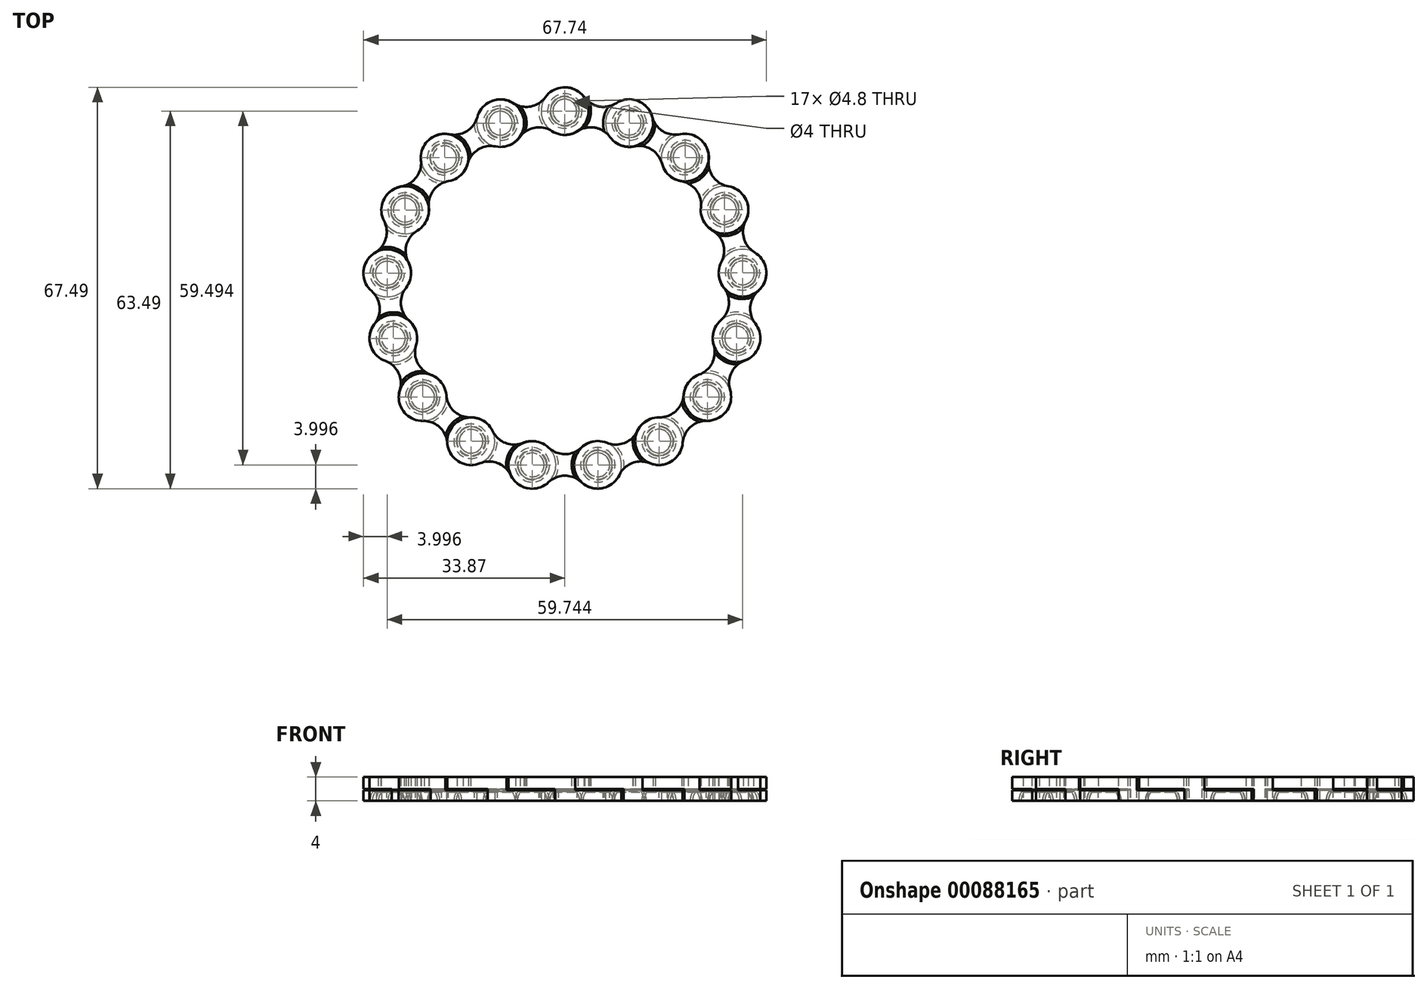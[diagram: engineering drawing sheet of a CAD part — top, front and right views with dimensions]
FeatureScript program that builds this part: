
annotation { "Feature Type Name" : "Feature", "Feature Type Description" : "" }
export const myFeature = defineFeature(function(context is Context, id is Id, definition is map)
    precondition{}
    {
        {
            var Q0;
            Q0=qCreatedBy(makeId("Top.planeOp"),FACE);
            var sketch = newSketch(context, id + "F0", { "sketchPlane" : qUnion([Q0])});
            skCircle(sketch, "E0", {"center": v(0, 0) * mm, "radius": 30 * mm, "construction": true});
            skCircle(sketch, "E1", {"center": v(0, 30) * mm, "radius": 4 * mm});
            skCircle(sketch, "E2", {"center": v(10.81, 27.98) * mm, "radius": 4 * mm});
            skArc(sketch, "E3", {"start": v(3.24, 32.35) * mm, "mid": v(5.74, 30.77) * mm, "end": v(8.64, 31.34) * mm});
            skArc(sketch, "E4", {"start": v(7.58, 25.63) * mm, "mid": v(5.08, 27.21) * mm, "end": v(2.17, 26.64) * mm});
            skCircle(sketch, "E5", {"center": v(0, 30) * mm, "radius": 2 * mm});
            skCircle(sketch, "E6", {"center": v(10.81, 27.98) * mm, "radius": 2 * mm});
            skSolve(sketch);
        }
        {
            var Q0;
            Q0 = qSketchRegion(id + "F0", true);
            var Q1;
            Q1=makeQuery(id+"F0.imprint","IMPRINT",FACE,{"disambiguationData":[TD([[makeQuery(id+"F0.imprint","IMPRINT",EDGE,{"derivedFrom":sQuery(id+"F0.wireOp",EDGE,"E6")}),1.0]])]});
            extrude(context, id + "F1", {"entities" : qUnion([Q0, Q1]), "depth" : 2 * mm});
        }
        {
            var Q0;
            Q0=makeQuery(id+"F0.imprint","IMPRINT",FACE,{"disambiguationData":[TD([[makeQuery(id+"F0.imprint","IMPRINT",EDGE,{"derivedFrom":sQuery(id+"F0.wireOp",EDGE,"E6")}),-1.0]])]});
            var Q1;
            Q1=makeQuery(id+"F0.imprint","IMPRINT",FACE,{"disambiguationData":[TD([[makeQuery(id+"F0.imprint","IMPRINT",EDGE,{"derivedFrom":sQuery(id+"F0.wireOp",EDGE,"E6")}),1.0]])]});
            var Q2;
            {var subQ0=sQuery(id+"F0.wireOp",EDGE,"E3");Q2=makeQuery(id+"F0.imprint","IMPRINT",FACE,{"disambiguationData":[TD([[makeQuery(id+"F0.imprint","IMPRINT",EDGE,{"derivedFrom":subQ0}),-1.0]])]});}
            extrude(context, id + "F2", {"entities" : qUnion([Q0, Q1, Q2]), "operationType" : NewBodyOperationType.ADD, "depth" : 4 * mm});
        }
        {
            var Q0;
            Q0=makeQuery(id+"F0.imprint","IMPRINT",FACE,{"disambiguationData":[TD([[makeQuery(id+"F0.imprint","IMPRINT",EDGE,{"derivedFrom":sQuery(id+"F0.wireOp",EDGE,"E6")}),1.0]])]});
            var sketch = newSketch(context, id + "F3", { "sketchPlane" : qUnion([Q0])});
            skArc(sketch, "E7", {"start": v(13.31, 27.98) * mm, "mid": v(10.81, 30.48) * mm, "end": v(8.31, 27.98) * mm});
            skLineSegment(sketch, "E8", {"start": v(13.31, 27.98) * mm, "end": v(8.31, 27.98) * mm});
            skSolve(sketch);
        }
        {
            var Q0;
            Q0=makeQuery(id+"F0.imprint","IMPRINT",FACE,{"disambiguationData":[TD([[makeQuery(id+"F0.imprint","IMPRINT",EDGE,{"derivedFrom":sQuery(id+"F0.wireOp",EDGE,"E6")}),-1.0]])]});
            extrude(context, id + "F4", {"entities" : qUnion([Q0]), "operationType" : NewBodyOperationType.REMOVE, "depth" : 2 * mm});
        }
        {
            var Q0;
            Q0 = qSketchRegion(id + "F3", true);
            var Q1;
            Q1=sQuery(id+"F3.wireOp",EDGE,"E8");
            revolve(context, id + "F5", {"operationType" : NewBodyOperationType.ADD, "entities" : qUnion([Q0]), "axis" : qUnion([Q1]), "revolveType" : RevolveType.ONE_DIRECTION, "oppositeDirection" : true, "angle" : 180 * degree});
        }
        {
            var Q0;
            Q0=makeQuery(id+"F2.opExtrude","CAP_FACE",FACE,{"disambiguationData":[OSD([sQuery(id+"F0.wireOp",EDGE,"E1"),sQuery(id+"F0.wireOp",EDGE,"E2"),sQuery(id+"F0.wireOp",EDGE,"E3"),sQuery(id+"F0.wireOp",EDGE,"E4")])],"isStart":false});
            var sketch = newSketch(context, id + "F6", { "sketchPlane" : qUnion([Q0])});
            skArc(sketch, "E9", {"start": v(13.31, 27.98) * mm, "mid": v(10.81, 30.48) * mm, "end": v(8.31, 27.98) * mm});
            skLineSegment(sketch, "E10", {"start": v(13.31, 27.98) * mm, "end": v(8.31, 27.98) * mm});
            skSolve(sketch);
        }
        {
            var Q0;
            {var subQ0=sQuery(id+"F0.wireOp",EDGE,"E3");Q0=makeQuery(id+"F0.imprint","IMPRINT",FACE,{"disambiguationData":[TD([[makeQuery(id+"F0.imprint","IMPRINT",EDGE,{"derivedFrom":subQ0}),-1.0]])]});}
            var sketch = newSketch(context, id + "F7", { "sketchPlane" : qUnion([Q0])});
            skCircle(sketch, "E11.0", {"center": v(10.81, 27.98) * mm, "radius": 4 * mm});
            skArc(sketch, "E12.0", {"start": v(7.58, 25.63) * mm, "mid": v(5.08, 27.21) * mm, "end": v(2.17, 26.64) * mm});
            skArc(sketch, "E13.0", {"start": v(3.24, 32.35) * mm, "mid": v(5.74, 30.77) * mm, "end": v(8.64, 31.34) * mm});
            skArc(sketch, "E14", {"start": v(7.45, 30.83) * mm, "mid": v(6.49, 28.79) * mm, "end": v(6.66, 26.54) * mm});
            skSolve(sketch);
        }
        {
            var Q0;
            {var subQ5=sQuery(id+"F7.wireOp",EDGE,"E14");Q0=makeQuery(id+"F7.imprint","IMPRINT",FACE,{"disambiguationData":[TD([[makeQuery(id+"F7.imprint","IMPRINT",EDGE,{"derivedFrom":subQ5}),1.0]])]});}
            extrude(context, id + "F8", {"entities" : qUnion([Q0]), "operationType" : NewBodyOperationType.REMOVE, "depth" : 2 * mm});
        }
        {
            var Q0;
            Q0=makeQuery(id+"F1.opExtrude","SWEPT_BODY",BODY,{"disambiguationData":[OSD([sQuery(id+"F0.wireOp",EDGE,"E1"),sQuery(id+"F0.wireOp",EDGE,"E2"),sQuery(id+"F0.wireOp",EDGE,"E3"),sQuery(id+"F0.wireOp",EDGE,"E4"),sQuery(id+"F0.wireOp",EDGE,"E5")])]});
            var Q1;
            Q1=sQuery(id+"F0.wireOp",EDGE,"E0");
            circularPattern(context, id + "F9", {"entities" : qUnion([Q0]), "axis" : qUnion([Q1]), "angle" : 21.18 * degree, "instanceCount" : 2, "oppositeDirection" : true});
        }
        {
            var Q0;
            Q0=makeQuery(id+"F1.opExtrude","SWEPT_BODY",BODY,{"disambiguationData":[OSD([sQuery(id+"F0.wireOp",EDGE,"E1"),sQuery(id+"F0.wireOp",EDGE,"E2"),sQuery(id+"F0.wireOp",EDGE,"E3"),sQuery(id+"F0.wireOp",EDGE,"E4"),sQuery(id+"F0.wireOp",EDGE,"E5")])]});
            var Q1;
            Q1=makeQuery(id+"F9.opPattern","COPY",BODY,{"derivedFrom":makeQuery(id+"F1.opExtrude","SWEPT_BODY",BODY,{"disambiguationData":[OSD([sQuery(id+"F0.wireOp",EDGE,"E1"),sQuery(id+"F0.wireOp",EDGE,"E2"),sQuery(id+"F0.wireOp",EDGE,"E3"),sQuery(id+"F0.wireOp",EDGE,"E4"),sQuery(id+"F0.wireOp",EDGE,"E5")])]}),"instanceName":"1"});
            var Q2;
            Q2=makeQuery(id+"F8.boolean.opBoolean","MERGE",FACE,{"derivedFrom":[makeQuery(id+"F4.boolean.opBoolean","COPY",FACE,{"derivedFrom":makeQuery(id+"F4.opExtrude","CAP_FACE",FACE,{"disambiguationData":[OSD([sQuery(id+"F0.wireOp",EDGE,"E2"),sQuery(id+"F0.wireOp",EDGE,"E6")])],"isStart":false})}),makeQuery(id+"F8.opExtrude","CAP_FACE",FACE,{"disambiguationData":[OSD([sQuery(id+"F7.wireOp",EDGE,"E11.0"),sQuery(id+"F7.wireOp",EDGE,"E12.0"),sQuery(id+"F7.wireOp",EDGE,"E13.0"),sQuery(id+"F7.wireOp",EDGE,"E14")])],"isStart":false})]});
            booleanBodies(context, id + "F10", {"operationType" : BooleanOperationType.SUBTRACTION, "tools" : qUnion([Q0]), "targets" : qUnion([Q1]), "offset" : true, "entitiesToOffset" : qUnion([Q2]), "offsetDistance" : .2 * mm, "keepTools" : true});
        }
        {
            var Q0;
            Q0=makeQuery(id+"F1.opExtrude","SWEPT_BODY",BODY,{"disambiguationData":[OSD([sQuery(id+"F0.wireOp",EDGE,"E1"),sQuery(id+"F0.wireOp",EDGE,"E2"),sQuery(id+"F0.wireOp",EDGE,"E3"),sQuery(id+"F0.wireOp",EDGE,"E4"),sQuery(id+"F0.wireOp",EDGE,"E5")])]});
            var Q1;
            Q1=makeQuery(id+"F9.opPattern","COPY",BODY,{"derivedFrom":makeQuery(id+"F1.opExtrude","SWEPT_BODY",BODY,{"disambiguationData":[OSD([sQuery(id+"F0.wireOp",EDGE,"E1"),sQuery(id+"F0.wireOp",EDGE,"E2"),sQuery(id+"F0.wireOp",EDGE,"E3"),sQuery(id+"F0.wireOp",EDGE,"E4"),sQuery(id+"F0.wireOp",EDGE,"E5")])]}),"instanceName":"1"});
            var Q2;
            {var subQ0=sQuery(id+"F0.wireOp",EDGE,"E2");Q2=makeQuery(id+"F2.boolean.opBoolean","MERGE",FACE,{"derivedFrom":[makeQuery(id+"F1.opExtrude","SWEPT_FACE",FACE,{"disambiguationData":[OSD([subQ0])]}),makeQuery(id+"F2.opExtrude","SWEPT_FACE",FACE,{"disambiguationData":[OSD([subQ0])]})]});}
            var Q3;
            Q3=makeQuery(id+"F4.boolean.opBoolean","COPY",FACE,{"derivedFrom":makeQuery(id+"F4.opExtrude","SWEPT_FACE",FACE,{"disambiguationData":[OSD([sQuery(id+"F0.wireOp",EDGE,"E6")])]})});
            var Q4;
            Q4=makeQuery(id+"F5.opRevolve","SWEPT_FACE",FACE,{"disambiguationData":[OSD([sQuery(id+"F3.wireOp",EDGE,"E7")])]});
            booleanBodies(context, id + "F11", {"operationType" : BooleanOperationType.SUBTRACTION, "tools" : qUnion([Q0]), "targets" : qUnion([Q1]), "offset" : true, "entitiesToOffset" : qUnion([Q2, Q3, Q4]), "offsetDistance" : .4 * mm, "keepTools" : true});
        }
        {
            var Q0;
            Q0=makeQuery(id+"F10.tempBoolean.opBoolean","COPY",FACE,{"derivedFrom":makeQuery(id+"F10.offsetTempBody.opPattern","COPY",FACE,{"derivedFrom":makeQuery(id+"F8.boolean.opBoolean","MERGE",FACE,{"derivedFrom":[makeQuery(id+"F4.boolean.opBoolean","COPY",FACE,{"derivedFrom":makeQuery(id+"F4.opExtrude","CAP_FACE",FACE,{"disambiguationData":[OSD([sQuery(id+"F0.wireOp",EDGE,"E2"),sQuery(id+"F0.wireOp",EDGE,"E6")])],"isStart":false})}),makeQuery(id+"F8.opExtrude","CAP_FACE",FACE,{"disambiguationData":[OSD([sQuery(id+"F7.wireOp",EDGE,"E11.0"),sQuery(id+"F7.wireOp",EDGE,"E12.0"),sQuery(id+"F7.wireOp",EDGE,"E13.0"),sQuery(id+"F7.wireOp",EDGE,"E14")])],"isStart":false})]}),"instanceName":"1"})});
            var sketch = newSketch(context, id + "F12", { "sketchPlane" : qUnion([Q0])});
            skArc(sketch, "E15.0", {"start": v(12.9, 24.11) * mm, "mid": v(14.56, 25.67) * mm, "end": v(15.21, 27.85) * mm});
            skCircle(sketch, "E16", {"center": v(10.81, 27.98) * mm, "radius": 4.4 * mm});
            skSolve(sketch);
        }
        {
            var Q0;
            Q0 = qSketchRegion(id + "F12", true);
            extrude(context, id + "F13", {"entities" : qUnion([Q0]), "operationType" : NewBodyOperationType.REMOVE, "depth" : 25 * mm});
        }
        {
            var Q0;
            Q0=makeQuery(id+"F9.opPattern","COPY",BODY,{"derivedFrom":makeQuery(id+"F1.opExtrude","SWEPT_BODY",BODY,{"disambiguationData":[OSD([sQuery(id+"F0.wireOp",EDGE,"E1"),sQuery(id+"F0.wireOp",EDGE,"E2"),sQuery(id+"F0.wireOp",EDGE,"E3"),sQuery(id+"F0.wireOp",EDGE,"E4"),sQuery(id+"F0.wireOp",EDGE,"E5")])]}),"instanceName":"1"});
            var Q1;
            Q1=sQuery(id+"F0.wireOp",EDGE,"E0");
            circularPattern(context, id + "F14", {"entities" : qUnion([Q0]), "axis" : qUnion([Q1]), "angle" : 21.18 * degree, "instanceCount" : 17});
        }
    });
